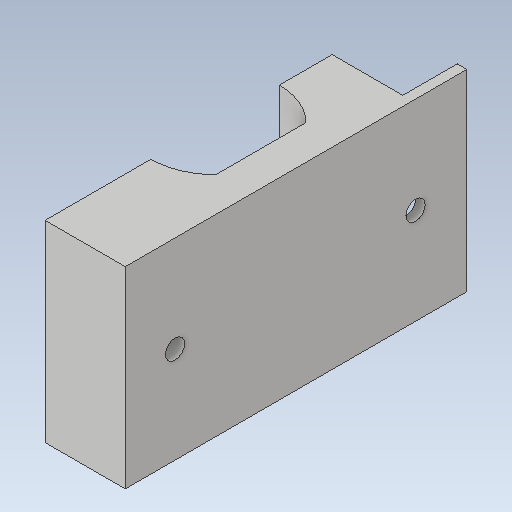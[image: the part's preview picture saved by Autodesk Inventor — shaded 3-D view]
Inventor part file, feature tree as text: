
AUTODESK INVENTOR PART (.ipt)
format: ipt  version: 2020.1 (Build 241239000, 239)  size: 168,448 bytes
history: native  units: mm
features: other x8, extrude x7, sketch x7, mirror x2
ambient origin geometry x8: Origin, YZ Plane, XZ Plane, XY Plane, X Axis, Y Axis, Z Axis, Center Point
bodies: Body1 (feature_tree)
feature tree (24):
  other  "Sólido1"
  extrude  "Extrusión1"  Depth=12.5mm
  extrude  "Extrusión2"  Depth=10.0mm
  extrude  "Extrusión3"  Depth=7.0mm
  extrude  "Extrusión4"  Depth=2.0mm
  mirror  "Simetría1"
  mirror  "Simetría2"
  extrude  "Extrusión5"  Depth=2.0mm TaperAngle=0.0deg
  other  "Edición directa1"
  other  "Edición directa2"
  extrude  "Extrusión6"  Depth=8.0mm TaperAngle=0.0deg
  other  "Edición directa3"
  extrude  "Extrusion7"  Depth=10.0mm
  sketch  "Boceto1"  dims[d0=55.0mm d1=12.5mm]
  sketch  "Boceto2"  dims[d2=30.0mm d3=0.0mm d5=10.0mm]
  sketch  "Boceto3"  dims[d6=30.0mm d7=0.0mm d8=7.0mm]
  sketch  "Boceto4"  dims[d9=2.0mm d10=0.0mm d11=7.5mm]
  sketch  "Boceto5"  dims[d12=2.0mm d13=0.0mm d14=2.0mm d15=0.0mm]
  sketch  "Boceto6"  dims[d16=0.0mm d17=0.0mm d18=6.0mm d19=0.0mm d20=0.0mm d21=8.0mm]
  sketch  "Sketch7"  dims[d22=15.0mm d23=3.0mm d24=3.0mm d25=12.5mm d26=0.0mm d27=0.0mm d28=0.0mm d29=-1.0mm d30=0.0mm d31=0.0mm d32=-0.75mm d33=11.0mm d34=8.5mm d35=10.0mm d36=0.0mm]
  other  "Desplazar1"
  other  "Desplazar2"
  other  "Desplazar3"
  other  "Desplazar4"
